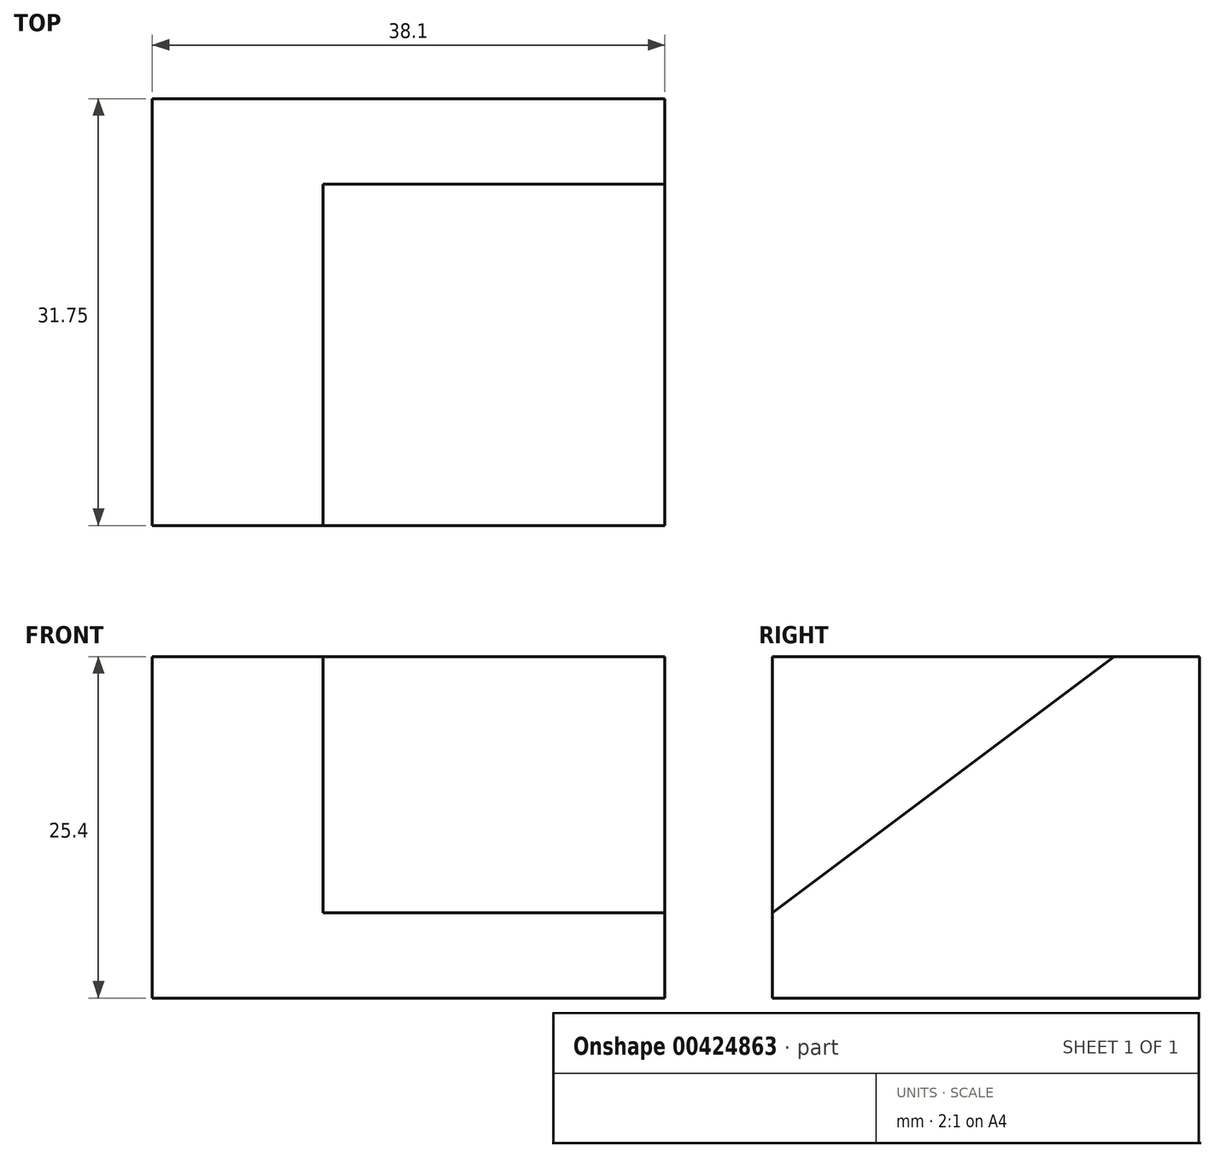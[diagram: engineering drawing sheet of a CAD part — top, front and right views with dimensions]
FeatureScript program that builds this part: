
annotation { "Feature Type Name" : "Feature", "Feature Type Description" : "" }
export const myFeature = defineFeature(function(context is Context, id is Id, definition is map)
    precondition{}
    {
        {
            var Q0;
            Q0=qCreatedBy(makeId("Top.planeOp"),FACE);
            var sketch = newSketch(context, id + "F0", { "sketchPlane" : qUnion([Q0])});
            skLineSegment(sketch, "E0", {"start": v(0, 0) * mm, "end": v(0, 31.75) * mm});
            skLineSegment(sketch, "E1", {"start": v(0, 31.75) * mm, "end": v(50.8, 31.75) * mm});
            skLineSegment(sketch, "E2", {"start": v(50.8, 31.75) * mm, "end": v(50.8, 0) * mm});
            skLineSegment(sketch, "E3", {"start": v(0, 0) * mm, "end": v(50.8, 0) * mm});
            skSolve(sketch);
        }
        {
            var Q0;
            Q0 = qSketchRegion(id + "F0", true);
            extrude(context, id + "F1", {"entities" : qUnion([Q0]), "depth" : 25.4 * mm});
        }
        {
            var Q0;
            Q0=makeQuery(id+"F1.opExtrude","SWEPT_FACE",FACE,{"disambiguationData":[OSD([sQuery(id+"F0.wireOp",EDGE,"E2")])]});
            var sketch = newSketch(context, id + "F2", { "sketchPlane" : qUnion([Q0])});
            skLineSegment(sketch, "E4", {"start": v(31.75, 25.4) * mm, "end": v(25.4, 25.4) * mm});
            skLineSegment(sketch, "E5", {"start": v(0, 0) * mm, "end": v(0, 6.35) * mm});
            skLineSegment(sketch, "E6", {"start": v(0, 6.35) * mm, "end": v(25.4, 25.4) * mm});
            skSolve(sketch);
        }
        {
            var Q0;
            {var subQ0=sQuery(id+"F2.wireOp",EDGE,"E6");Q0=makeQuery(id+"F2.imprint","IMPRINT",FACE,{"disambiguationData":[TD([[makeQuery(id+"F2.imprint","IMPRINT",EDGE,{"derivedFrom":subQ0}),1.0]])]});}
            extrude(context, id + "F3", {"entities" : qUnion([Q0]), "operationType" : NewBodyOperationType.REMOVE, "oppositeDirection" : true, "depth" : 25.4 * mm});
        }
        {
            var Q0;
            Q0=makeQuery(id+"F1.opExtrude","SWEPT_FACE",FACE,{"disambiguationData":[OSD([sQuery(id+"F0.wireOp",EDGE,"E0")])]});
            extrude(context, id + "F4", {"entities" : qUnion([Q0]), "operationType" : NewBodyOperationType.REMOVE, "oppositeDirection" : true, "depth" : 6.35 * mm});
        }
        {
            var Q0;
            Q0=makeQuery(id+"F4.boolean.opBoolean","COPY",FACE,{"derivedFrom":makeQuery(id+"F4.opExtrude","CAP_FACE",FACE,{"disambiguationData":[OSD([sQuery(id+"F0.wireOp",EDGE,"E0")])],"isStart":false})});
            extrude(context, id + "F5", {"entities" : qUnion([Q0]), "operationType" : NewBodyOperationType.REMOVE, "oppositeDirection" : true, "depth" : 6.35 * mm});
        }
    });
